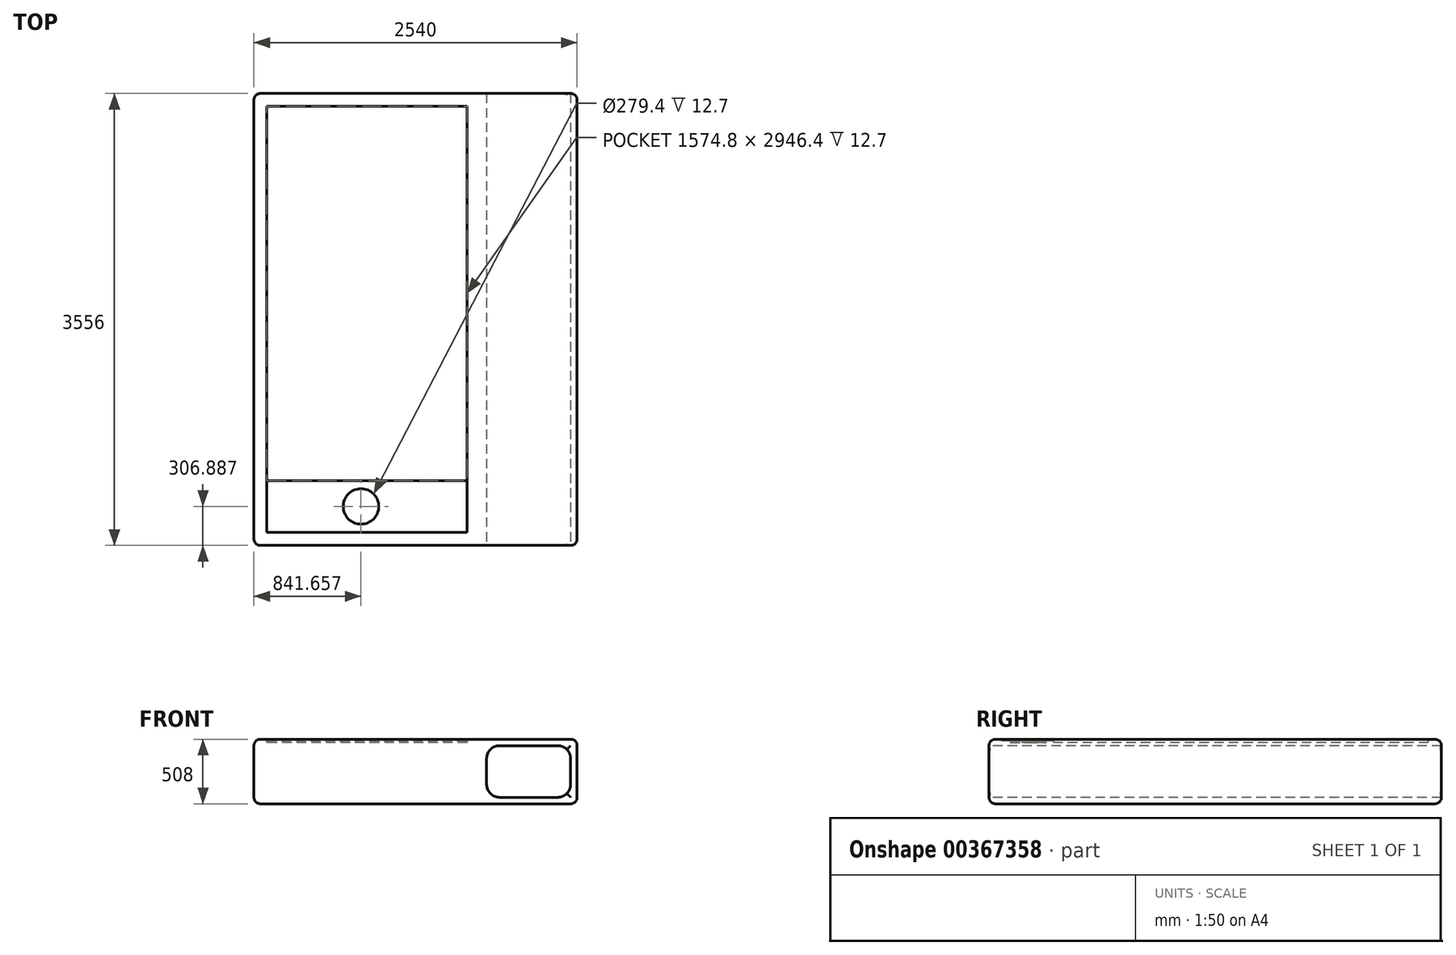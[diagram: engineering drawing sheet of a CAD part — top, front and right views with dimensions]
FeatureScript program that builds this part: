
annotation { "Feature Type Name" : "Feature", "Feature Type Description" : "" }
export const myFeature = defineFeature(function(context is Context, id is Id, definition is map)
    precondition{}
    {
        {
            var Q0;
            Q0=qCreatedBy(makeId("Top.planeOp"),FACE);
            var sketch = newSketch(context, id + "F0", { "sketchPlane" : qUnion([Q0])});
            skLineSegment(sketch, "E0.bottom", {"start": v(0, 0) * mm, "end": v(1778, 0) * mm});
            skLineSegment(sketch, "E0.top", {"start": v(0, 3556) * mm, "end": v(1778, 3556) * mm});
            skLineSegment(sketch, "E0.left", {"start": v(0, 0) * mm, "end": v(0, 3556) * mm});
            skLineSegment(sketch, "E0.right", {"start": v(1778, 0) * mm, "end": v(1778, 3556) * mm});
            skLineSegment(sketch, "E1.bottom", {"start": v(1778, 3556) * mm, "end": v(2540, 3556) * mm});
            skLineSegment(sketch, "E1.top", {"start": v(1778, 0) * mm, "end": v(2540, 0) * mm});
            skLineSegment(sketch, "E1.left", {"start": v(1778, 3556) * mm, "end": v(1778, 0) * mm});
            skLineSegment(sketch, "E1.right", {"start": v(2540, 3556) * mm, "end": v(2540, 0) * mm});
            skSolve(sketch);
        }
        {
            var Q0;
            Q0=makeQuery(id+"F0.imprint","IMPRINT",FACE,{"disambiguationData":[TD([[makeQuery(id+"F0.imprint","IMPRINT",EDGE,{"derivedFrom":sQuery(id+"F0.wireOp",EDGE,"E0.bottom")}),1.0]])]});
            var Q1;
            Q1=makeQuery(id+"F0.imprint","IMPRINT",FACE,{"disambiguationData":[TD([[makeQuery(id+"F0.imprint","IMPRINT",EDGE,{"derivedFrom":sQuery(id+"F0.wireOp",EDGE,"E0.right")}),-1.0]])]});
            extrude(context, id + "F1", {"entities" : qUnion([Q0, Q1]), "depth" : 508 * mm, "offsetDistance" : 25.4 * mm});
        }
        {
            var Q0;
            Q0=makeQuery(id+"F1.opExtrude","SWEPT_FACE",FACE,{"disambiguationData":[OSD([sQuery(id+"F0.wireOp",EDGE,"E0.bottom"),sQuery(id+"F0.wireOp",EDGE,"E1.top")])]});
            var sketch = newSketch(context, id + "F2", { "sketchPlane" : qUnion([Q0])});
            skLineSegment(sketch, "E2.bottom", {"start": v(2540, 508) * mm, "end": v(1778, 508) * mm});
            skLineSegment(sketch, "E2.top", {"start": v(2540, 0) * mm, "end": v(1778, 0) * mm});
            skLineSegment(sketch, "E2.left", {"start": v(2540, 508) * mm, "end": v(2540, 0) * mm});
            skLineSegment(sketch, "E2.right", {"start": v(1778, 508) * mm, "end": v(1778, 0) * mm});
            skLineSegment(sketch, "E3.0", {"start": v(2489.2, 457.2) * mm, "end": v(1828.8, 457.2) * mm});
            skLineSegment(sketch, "E3.1", {"start": v(2489.2, 457.2) * mm, "end": v(2489.2, 50.8) * mm});
            skLineSegment(sketch, "E3.2", {"start": v(2489.2, 50.8) * mm, "end": v(1828.8, 50.8) * mm});
            skLineSegment(sketch, "E3.3", {"start": v(1828.8, 457.2) * mm, "end": v(1828.8, 50.8) * mm});
            skSolve(sketch);
        }
        {
            var Q0;
            Q0=makeQuery(id+"F2.imprint","IMPRINT",FACE,{"disambiguationData":[TD([[makeQuery(id+"F2.imprint","IMPRINT",EDGE,{"derivedFrom":sQuery(id+"F2.wireOp",EDGE,"E3.0")}),1.0]])]});
            extrude(context, id + "F3", {"entities" : qUnion([Q0]), "operationType" : NewBodyOperationType.REMOVE, "oppositeDirection" : true, "depth" : 3556 * mm, "offsetDistance" : 25.4 * mm});
        }
        {
            var Q0;
            Q0=makeQuery(id+"F1.opExtrude","CAP_FACE",FACE,{"disambiguationData":[OSD([sQuery(id+"F0.wireOp",EDGE,"E0.bottom"),sQuery(id+"F0.wireOp",EDGE,"E0.top"),sQuery(id+"F0.wireOp",EDGE,"E0.left"),sQuery(id+"F0.wireOp",EDGE,"E1.bottom"),sQuery(id+"F0.wireOp",EDGE,"E1.top"),sQuery(id+"F0.wireOp",EDGE,"E1.right")])],"isStart":false});
            var sketch = newSketch(context, id + "F4", { "sketchPlane" : qUnion([Q0])});
            skLineSegment(sketch, "E4.bottom", {"start": v(0, 3556) * mm, "end": v(1778, 3556) * mm});
            skLineSegment(sketch, "E4.top", {"start": v(0, 0) * mm, "end": v(1778, 0) * mm});
            skLineSegment(sketch, "E4.left", {"start": v(0, 3556) * mm, "end": v(0, 0) * mm});
            skLineSegment(sketch, "E4.right", {"start": v(1778, 3556) * mm, "end": v(1778, 0) * mm});
            skLineSegment(sketch, "E5.0", {"start": v(101.6, 3454.4) * mm, "end": v(101.6, 101.6) * mm});
            skLineSegment(sketch, "E5.1", {"start": v(101.6, 3454.4) * mm, "end": v(1676.4, 3454.4) * mm});
            skLineSegment(sketch, "E5.2", {"start": v(1676.4, 3454.4) * mm, "end": v(1676.4, 101.6) * mm});
            skLineSegment(sketch, "E5.3", {"start": v(101.6, 101.6) * mm, "end": v(1676.4, 101.6) * mm});
            skSolve(sketch);
        }
        {
            var Q0;
            Q0=makeQuery(id+"F4.imprint","IMPRINT",FACE,{"disambiguationData":[TD([[makeQuery(id+"F4.imprint","IMPRINT",EDGE,{"derivedFrom":sQuery(id+"F4.wireOp",EDGE,"E5.0")}),1.0]])]});
            extrude(context, id + "F5", {"entities" : qUnion([Q0]), "operationType" : NewBodyOperationType.REMOVE, "oppositeDirection" : true, "depth" : 25.4 * mm, "offsetDistance" : 25.4 * mm});
        }
        {
            var Q0;
            Q0=makeQuery(id+"F1.opExtrude","SWEPT_EDGE",EDGE,{"disambiguationData":[OSD([sQuery(id+"F0.wireOp",EDGE,"E1.top"),sQuery(id+"F0.wireOp",EDGE,"E1.right")])]});
            var Q1;
            Q1=makeQuery(id+"F1.opExtrude","CAP_EDGE",EDGE,{"disambiguationData":[OSD([sQuery(id+"F0.wireOp",EDGE,"E0.bottom"),sQuery(id+"F0.wireOp",EDGE,"E1.top")])],"isStart":true});
            var Q2;
            Q2=makeQuery(id+"F1.opExtrude","CAP_EDGE",EDGE,{"disambiguationData":[OSD([sQuery(id+"F0.wireOp",EDGE,"E1.right")])],"isStart":true});
            var Q3;
            Q3=makeQuery(id+"F1.opExtrude","CAP_EDGE",EDGE,{"disambiguationData":[OSD([sQuery(id+"F0.wireOp",EDGE,"E1.right")])],"isStart":false});
            var Q4;
            Q4=makeQuery(id+"F1.opExtrude","SWEPT_EDGE",EDGE,{"disambiguationData":[OSD([sQuery(id+"F0.wireOp",EDGE,"E1.bottom"),sQuery(id+"F0.wireOp",EDGE,"E1.right")])]});
            var Q5;
            Q5=makeQuery(id+"F1.opExtrude","CAP_EDGE",EDGE,{"disambiguationData":[OSD([sQuery(id+"F0.wireOp",EDGE,"E0.top"),sQuery(id+"F0.wireOp",EDGE,"E1.bottom")])],"isStart":false});
            var Q6;
            Q6=makeQuery(id+"F1.opExtrude","CAP_EDGE",EDGE,{"disambiguationData":[OSD([sQuery(id+"F0.wireOp",EDGE,"E0.left")])],"isStart":false});
            var Q7;
            Q7=makeQuery(id+"F1.opExtrude","CAP_EDGE",EDGE,{"disambiguationData":[OSD([sQuery(id+"F0.wireOp",EDGE,"E0.left")])],"isStart":true});
            var Q8;
            Q8=makeQuery(id+"F1.opExtrude","SWEPT_EDGE",EDGE,{"disambiguationData":[OSD([sQuery(id+"F0.wireOp",EDGE,"E0.top"),sQuery(id+"F0.wireOp",EDGE,"E0.left")])]});
            var Q9;
            Q9=makeQuery(id+"F1.opExtrude","CAP_EDGE",EDGE,{"disambiguationData":[OSD([sQuery(id+"F0.wireOp",EDGE,"E0.top"),sQuery(id+"F0.wireOp",EDGE,"E1.bottom")])],"isStart":true});
            var Q10;
            Q10=makeQuery(id+"F1.opExtrude","CAP_EDGE",EDGE,{"disambiguationData":[OSD([sQuery(id+"F0.wireOp",EDGE,"E0.bottom"),sQuery(id+"F0.wireOp",EDGE,"E1.top")])],"isStart":false});
            var Q11;
            Q11=makeQuery(id+"F1.opExtrude","SWEPT_EDGE",EDGE,{"disambiguationData":[OSD([sQuery(id+"F0.wireOp",EDGE,"E0.bottom"),sQuery(id+"F0.wireOp",EDGE,"E0.left")])]});
            fillet(context, id + "F6", {"entities" : qUnion([Q0, Q1, Q2, Q3, Q4, Q5, Q6, Q7, Q8, Q9, Q10, Q11]), "tangentPropagation" : true, "radius" : 50.8 * mm, "defaultsChanged" : true, "vertexSettings" : [], "allowEdgeOverflow" : false});
        }
        {
            var Q0;
            Q0=makeQuery(id+"F3.boolean.opBoolean","COPY",EDGE,{"derivedFrom":makeQuery(id+"F3.opExtrude","SWEPT_EDGE",EDGE,{"disambiguationData":[OSD([sQuery(id+"F2.wireOp",EDGE,"E3.2"),sQuery(id+"F2.wireOp",EDGE,"E3.3")])]})});
            var Q1;
            Q1=makeQuery(id+"F3.boolean.opBoolean","COPY",EDGE,{"derivedFrom":makeQuery(id+"F3.opExtrude","SWEPT_EDGE",EDGE,{"disambiguationData":[OSD([sQuery(id+"F2.wireOp",EDGE,"E3.1"),sQuery(id+"F2.wireOp",EDGE,"E3.2")])]})});
            var Q2;
            Q2=makeQuery(id+"F3.boolean.opBoolean","COPY",EDGE,{"derivedFrom":makeQuery(id+"F3.opExtrude","SWEPT_EDGE",EDGE,{"disambiguationData":[OSD([sQuery(id+"F2.wireOp",EDGE,"E3.0"),sQuery(id+"F2.wireOp",EDGE,"E3.1")])]})});
            var Q3;
            Q3=makeQuery(id+"F3.boolean.opBoolean","COPY",EDGE,{"derivedFrom":makeQuery(id+"F3.opExtrude","SWEPT_EDGE",EDGE,{"disambiguationData":[OSD([sQuery(id+"F2.wireOp",EDGE,"E3.0"),sQuery(id+"F2.wireOp",EDGE,"E3.3")])]})});
            fillet(context, id + "F7", {"entities" : qUnion([Q0, Q1, Q2, Q3]), "tangentPropagation" : true, "radius" : 101.6 * mm, "defaultsChanged" : true, "vertexSettings" : [], "allowEdgeOverflow" : false});
        }
        {
            var Q0;
            Q0=makeQuery(id+"F5.boolean.opBoolean","COPY",FACE,{"derivedFrom":makeQuery(id+"F5.opExtrude","CAP_FACE",FACE,{"disambiguationData":[OSD([sQuery(id+"F4.wireOp",EDGE,"E5.0"),sQuery(id+"F4.wireOp",EDGE,"E5.1"),sQuery(id+"F4.wireOp",EDGE,"E5.2"),sQuery(id+"F4.wireOp",EDGE,"E5.3")])],"isStart":false})});
            var sketch = newSketch(context, id + "F8", { "sketchPlane" : qUnion([Q0])});
            skLineSegment(sketch, "E6.bottom", {"start": v(1676.4, 101.6) * mm, "end": v(101.6, 101.6) * mm});
            skLineSegment(sketch, "E6.top", {"start": v(1676.4, 508) * mm, "end": v(101.6, 508) * mm});
            skLineSegment(sketch, "E6.left", {"start": v(1676.4, 101.6) * mm, "end": v(1676.4, 508) * mm});
            skLineSegment(sketch, "E6.right", {"start": v(101.6, 101.6) * mm, "end": v(101.6, 508) * mm});
            skCircle(sketch, "E7", {"center": v(841.66, 306.89) * mm, "radius": 139.7 * mm});
            skSolve(sketch);
        }
        {
            var Q0;
            Q0=makeQuery(id+"F8.imprint","IMPRINT",FACE,{"disambiguationData":[TD([[makeQuery(id+"F8.imprint","IMPRINT",EDGE,{"derivedFrom":sQuery(id+"F8.wireOp",EDGE,"E6.bottom")}),1.0]])]});
            extrude(context, id + "F9", {"entities" : qUnion([Q0]), "operationType" : NewBodyOperationType.ADD, "depth" : 12.7 * mm, "offsetDistance" : 25.4 * mm});
        }
    });
